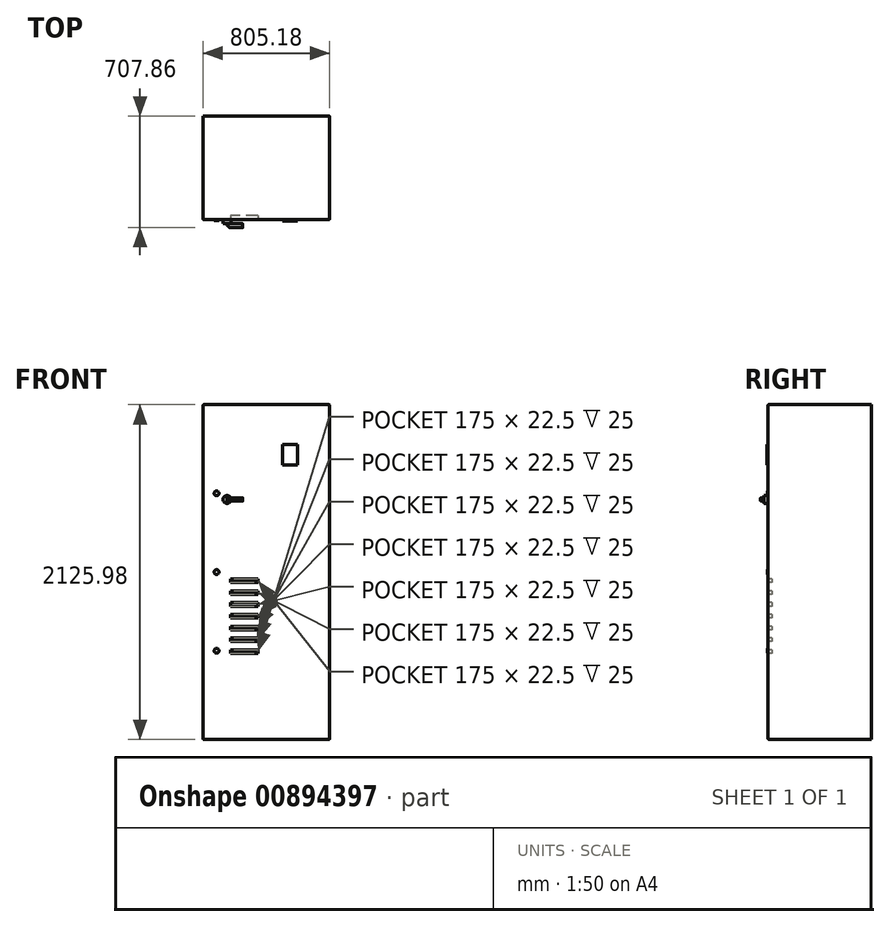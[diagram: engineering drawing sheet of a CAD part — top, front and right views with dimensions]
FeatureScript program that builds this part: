
annotation { "Feature Type Name" : "Feature", "Feature Type Description" : "" }
export const myFeature = defineFeature(function(context is Context, id is Id, definition is map)
    precondition{}
    {
        {
            var Q0;
            Q0=qCreatedBy(makeId("Front.planeOp"),FACE);
            var sketch = newSketch(context, id + "F0", { "sketchPlane" : qUnion([Q0])});
            skLineSegment(sketch, "E0.bottom", {"start": v(402.6, 1063) * mm, "end": v(-402.59, 1063) * mm});
            skLineSegment(sketch, "E0.top", {"start": v(402.59, -1063) * mm, "end": v(-402.6, -1063) * mm});
            skLineSegment(sketch, "E0.left", {"start": v(402.6, 1063) * mm, "end": v(402.59, -1063) * mm});
            skLineSegment(sketch, "E0.right", {"start": v(-402.59, 1063) * mm, "end": v(-402.6, -1063) * mm});
            skPoint(sketch, "E0.middle", {"position": v(0, 0) * mm});
            skSolve(sketch);
        }
        {
            var Q0;
            Q0 = qSketchRegion(id + "F0", true);
            extrude(context, id + "F1", {"entities" : qUnion([Q0]), "depth" : 657.86 * mm, "offsetDistance" : 25 * mm});
        }
        {
            var Q0;
            Q0=makeQuery(id+"F1.opExtrude","CAP_FACE",FACE,{"disambiguationData":[OSD([sQuery(id+"F0.wireOp",EDGE,"E0.bottom"),sQuery(id+"F0.wireOp",EDGE,"E0.top"),sQuery(id+"F0.wireOp",EDGE,"E0.left"),sQuery(id+"F0.wireOp",EDGE,"E0.right")])],"isStart":false});
            var sketch = newSketch(context, id + "F2", { "sketchPlane" : qUnion([Q0])});
            skCircle(sketch, "E1", {"center": v(-250.19, 461.01) * mm, "radius": 25 * mm});
            skSolve(sketch);
        }
        {
            var Q0;
            Q0 = qSketchRegion(id + "F2", true);
            extrude(context, id + "F3", {"entities" : qUnion([Q0]), "depth" : 25 * mm, "offsetDistance" : 25 * mm});
        }
        {
            var Q0;
            Q0=makeQuery(id+"F3.opExtrude","CAP_FACE",FACE,{"disambiguationData":[OSD([sQuery(id+"F2.wireOp",EDGE,"E1")])],"isStart":false});
            var sketch = newSketch(context, id + "F4", { "sketchPlane" : qUnion([Q0])});
            skLineSegment(sketch, "E2", {"start": v(-250.19, 461.01) * mm, "end": v(-250.19, 471.01) * mm});
            skLineSegment(sketch, "E3", {"start": v(-250.19, 471.01) * mm, "end": v(-149.7, 471.01) * mm});
            skLineSegment(sketch, "E4", {"start": v(-149.7, 471.01) * mm, "end": v(-149.7, 451.01) * mm});
            skLineSegment(sketch, "E5", {"start": v(-149.7, 451.01) * mm, "end": v(-250.19, 451.01) * mm});
            skLineSegment(sketch, "E6", {"start": v(-250.19, 451.01) * mm, "end": v(-250.19, 461.01) * mm});
            skSolve(sketch);
        }
        {
            var Q0;
            Q0 = qSketchRegion(id + "F4", true);
            extrude(context, id + "F5", {"entities" : qUnion([Q0]), "operationType" : NewBodyOperationType.ADD, "depth" : 25 * mm, "offsetDistance" : 25 * mm});
        }
        {
            var Q0;
            Q0=makeQuery(id+"F5.opExtrude","CAP_EDGE",EDGE,{"disambiguationData":[OSD([sQuery(id+"F4.wireOp",EDGE,"E2"),sQuery(id+"F4.wireOp",EDGE,"E6")])],"isStart":false});
            chamfer(context, id + "F6", {"entities" : qUnion([Q0]), "width" : 15 * mm, "tangentPropagation" : true});
        }
        {
            var Q0;
            {var subQ0=sQuery(id+"F4.wireOp",EDGE,"E5");Q0=makeQuery(id+"F5.boolean.opBoolean","SPLIT",EDGE,{"disambiguationData":[topologyDisambiguationEdgeConnected([makeQuery(id+"F3.opExtrude","CAP_FACE",FACE,{"disambiguationData":[OSD([sQuery(id+"F2.wireOp",EDGE,"E1")])],"isStart":false})])],"derivedFrom":makeQuery(id+"F5.opExtrude","CAP_EDGE",EDGE,{"disambiguationData":[OSD([subQ0])],"isStart":true})});}
            var Q1;
            Q1=makeQuery(id+"F5.opExtrude","CAP_EDGE",EDGE,{"disambiguationData":[OSD([sQuery(id+"F4.wireOp",EDGE,"E2"),sQuery(id+"F4.wireOp",EDGE,"E6")])],"isStart":true});
            var Q2;
            {var subQ0=sQuery(id+"F4.wireOp",EDGE,"E3");Q2=makeQuery(id+"F5.boolean.opBoolean","SPLIT",EDGE,{"disambiguationData":[topologyDisambiguationEdgeConnected([makeQuery(id+"F3.opExtrude","CAP_FACE",FACE,{"disambiguationData":[OSD([sQuery(id+"F2.wireOp",EDGE,"E1")])],"isStart":false})])],"derivedFrom":makeQuery(id+"F5.opExtrude","CAP_EDGE",EDGE,{"disambiguationData":[OSD([subQ0])],"isStart":true})});}
            var Q3;
            Q3=makeQuery(id+"F5.opExtrude","CAP_EDGE",EDGE,{"disambiguationData":[OSD([sQuery(id+"F4.wireOp",EDGE,"E3")])],"isStart":false});
            var Q4;
            Q4=makeQuery(id+"F5.opExtrude","CAP_EDGE",EDGE,{"disambiguationData":[OSD([sQuery(id+"F4.wireOp",EDGE,"E5")])],"isStart":false});
            var Q5;
            {var subQ0=sQuery(id+"F4.wireOp",EDGE,"E6");var subQ1=sQuery(id+"F4.wireOp",EDGE,"E2");Q5=makeQuery(id+"F6.opChamfer","BLEND_EDGE",EDGE,{"blendedFrom":[makeQuery(id+"F5.opExtrude","CAP_EDGE",EDGE,{"disambiguationData":[OSD([subQ1,subQ0])],"isStart":false}),makeQuery(id+"F5.opExtrude","CAP_FACE",FACE,{"disambiguationData":[OSD([subQ1,sQuery(id+"F4.wireOp",EDGE,"E3"),sQuery(id+"F4.wireOp",EDGE,"E4"),sQuery(id+"F4.wireOp",EDGE,"E5"),subQ0])],"isStart":false})],"blendedInto":[makeQuery(id+"F5.opExtrude","CAP_FACE",FACE,{"disambiguationData":[OSD([subQ1,sQuery(id+"F4.wireOp",EDGE,"E3"),sQuery(id+"F4.wireOp",EDGE,"E4"),sQuery(id+"F4.wireOp",EDGE,"E5"),subQ0])],"isStart":false})]});}
            var Q6;
            {var subQ0=sQuery(id+"F4.wireOp",EDGE,"E6");var subQ1=sQuery(id+"F4.wireOp",EDGE,"E2");Q6=makeQuery(id+"F6.opChamfer","BLEND_EDGE",EDGE,{"blendedFrom":[makeQuery(id+"F5.opExtrude","CAP_EDGE",EDGE,{"disambiguationData":[OSD([subQ1,subQ0])],"isStart":false}),makeQuery(id+"F5.opExtrude","SWEPT_FACE",FACE,{"disambiguationData":[OSD([subQ1,subQ0])]})],"blendedInto":[makeQuery(id+"F5.opExtrude","SWEPT_FACE",FACE,{"disambiguationData":[OSD([subQ1,subQ0])]})]});}
            fillet(context, id + "F7", {"entities" : qUnion([Q0, Q1, Q2, Q3, Q4, Q5, Q6]), "radius" : 5 * mm, "tangentPropagation" : true, "allowEdgeOverflow" : false});
        }
        {
            var Q0;
            Q0=makeQuery(id+"F1.opExtrude","CAP_FACE",FACE,{"disambiguationData":[OSD([sQuery(id+"F0.wireOp",EDGE,"E0.bottom"),sQuery(id+"F0.wireOp",EDGE,"E0.top"),sQuery(id+"F0.wireOp",EDGE,"E0.left"),sQuery(id+"F0.wireOp",EDGE,"E0.right")])],"isStart":true});
            var sketch = newSketch(context, id + "F8", { "sketchPlane" : qUnion([Q0])});
            skLineSegment(sketch, "E7.bottom", {"start": v(356.25, 606) * mm, "end": v(300, 606) * mm});
            skLineSegment(sketch, "E7.top", {"start": v(356.25, -606) * mm, "end": v(305, -606) * mm});
            skLineSegment(sketch, "E7.left", {"start": v(356.25, 606) * mm, "end": v(356.25, -606) * mm});
            skLineSegment(sketch, "E7.right", {"start": v(-356.25, 606) * mm, "end": v(-356.25, -606) * mm});
            skPoint(sketch, "E7.middle", {"position": v(0, 0) * mm});
            skLineSegment(sketch, "E8", {"start": v(0, 665.64) * mm, "end": v(0, -668.18) * mm, "construction": true});
            skLineSegment(sketch, "E9.bottom", {"start": v(300, 647.98) * mm, "end": v(-300, 647.98) * mm, "construction": true});
            skLineSegment(sketch, "E9.top", {"start": v(300, -647.98) * mm, "end": v(-300, -647.98) * mm, "construction": true});
            skLineSegment(sketch, "E9.left", {"start": v(300, 647.98) * mm, "end": v(300, -647.98) * mm, "construction": true});
            skLineSegment(sketch, "E9.right", {"start": v(-300, 647.98) * mm, "end": v(-300, -647.98) * mm, "construction": true});
            skLineSegment(sketch, "E10.left", {"start": v(-295, -606) * mm, "end": v(-295, -591) * mm});
            skLineSegment(sketch, "E10.right", {"start": v(-305, -606) * mm, "end": v(-305, -591) * mm});
            skPoint(sketch, "E10.middle", {"position": v(-300, -598.5) * mm});
            skArc(sketch, "E11", {"start": v(-305, -591) * mm, "mid": v(-300, -586) * mm, "end": v(-295, -591) * mm});
            skLineSegment(sketch, "E12.trimOffspring", {"start": v(-305, -606) * mm, "end": v(-356.25, -606) * mm});
            skLineSegment(sketch, "E13.MirrorCS", {"start": v(295, -606) * mm, "end": v(300, -606) * mm});
            skLineSegment(sketch, "E14.MirrorCS", {"start": v(305, -606) * mm, "end": v(305, -591) * mm});
            skLineSegment(sketch, "E15.MirrorCS", {"start": v(300, -606) * mm, "end": v(295, -606) * mm});
            skArc(sketch, "E16.MirrorCS", {"start": v(305, -591) * mm, "mid": v(300, -586) * mm, "end": v(295, -591) * mm});
            skLineSegment(sketch, "E17.MirrorCS", {"start": v(295, -606) * mm, "end": v(295, -591) * mm});
            skPoint(sketch, "E18.MirrorP", {"position": v(300, -598.5) * mm});
            skLineSegment(sketch, "E19.MirrorCS", {"start": v(-300, 606) * mm, "end": v(-305, 606) * mm});
            skLineSegment(sketch, "E20.MirrorCS", {"start": v(305, 606) * mm, "end": v(300, 606) * mm});
            skArc(sketch, "E21.MirrorCS", {"start": v(305, 591) * mm, "mid": v(300, 586) * mm, "end": v(295, 591) * mm});
            skLineSegment(sketch, "E22.MirrorCS", {"start": v(295, 606) * mm, "end": v(295, 591) * mm});
            skArc(sketch, "E23.MirrorCS", {"start": v(-305, 591) * mm, "mid": v(-300, 586) * mm, "end": v(-295, 591) * mm});
            skLineSegment(sketch, "E24.MirrorCS", {"start": v(-305, 606) * mm, "end": v(-305, 591) * mm});
            skLineSegment(sketch, "E25.MirrorCS", {"start": v(300, 606) * mm, "end": v(305, 606) * mm});
            skLineSegment(sketch, "E26.MirrorCS", {"start": v(-305, 606) * mm, "end": v(-300, 606) * mm});
            skLineSegment(sketch, "E27.MirrorCS", {"start": v(-295, 606) * mm, "end": v(-295, 591) * mm});
            skLineSegment(sketch, "E28.MirrorCS", {"start": v(305, 606) * mm, "end": v(305, 591) * mm});
            skPoint(sketch, "E29.MirrorP", {"position": v(300, 598.5) * mm});
            skPoint(sketch, "E30.MirrorP", {"position": v(-300, 598.5) * mm});
            skLineSegment(sketch, "E31.trimOffspring", {"start": v(300, -606) * mm, "end": v(-295, -606) * mm});
            skLineSegment(sketch, "E32.trimOffspring", {"start": v(295, 606) * mm, "end": v(-295, 606) * mm});
            skLineSegment(sketch, "E33.trimOffspring", {"start": v(-300, 606) * mm, "end": v(-356.25, 606) * mm});
            skPoint(sketch, "E34.orphan", {"position": v(-295, 606) * mm});
            skSolve(sketch);
        }
        {
            var Q0;
            Q0=makeQuery(id+"F1.opExtrude","CAP_FACE",FACE,{"disambiguationData":[OSD([sQuery(id+"F0.wireOp",EDGE,"E0.bottom"),sQuery(id+"F0.wireOp",EDGE,"E0.top"),sQuery(id+"F0.wireOp",EDGE,"E0.left"),sQuery(id+"F0.wireOp",EDGE,"E0.right")])],"isStart":false});
            var sketch = newSketch(context, id + "F9", { "sketchPlane" : qUnion([Q0])});
            skLineSegment(sketch, "E35.bottom", {"start": v(199.39, 809) * mm, "end": v(103.48, 809) * mm});
            skLineSegment(sketch, "E35.top", {"start": v(199.39, 681.5) * mm, "end": v(103.48, 681.5) * mm});
            skLineSegment(sketch, "E35.left", {"start": v(199.4, 809) * mm, "end": v(199.4, 681.5) * mm});
            skLineSegment(sketch, "E35.right", {"start": v(103.48, 809) * mm, "end": v(103.48, 681.5) * mm});
            skPoint(sketch, "E35.middle", {"position": v(151.43, 745.25) * mm});
            skSolve(sketch);
        }
        {
            var Q0;
            Q0 = qSketchRegion(id + "F9", true);
            extrude(context, id + "F10", {"entities" : qUnion([Q0]), "depth" : 7.5 * mm, "offsetDistance" : 25 * mm});
        }
        {
            var Q0;
            Q0=makeQuery(id+"F1.opExtrude","CAP_FACE",FACE,{"disambiguationData":[OSD([sQuery(id+"F0.wireOp",EDGE,"E0.bottom"),sQuery(id+"F0.wireOp",EDGE,"E0.top"),sQuery(id+"F0.wireOp",EDGE,"E0.left"),sQuery(id+"F0.wireOp",EDGE,"E0.right")])],"isStart":false});
            var sketch = newSketch(context, id + "F11", { "sketchPlane" : qUnion([Q0])});
            skLineSegment(sketch, "E36.bottom", {"start": v(-53.17, -44.51) * mm, "end": v(-228.17, -44.51) * mm});
            skLineSegment(sketch, "E36.top", {"start": v(-53.17, -67.01) * mm, "end": v(-228.17, -67.01) * mm});
            skLineSegment(sketch, "E36.left", {"start": v(-53.17, -44.51) * mm, "end": v(-53.17, -67.01) * mm});
            skLineSegment(sketch, "E36.right", {"start": v(-228.17, -44.51) * mm, "end": v(-228.17, -67.01) * mm});
            skPoint(sketch, "E36.middle", {"position": v(-140.67, -55.76) * mm});
            skLineSegment(sketch, "E37.0.1.0", {"start": v(-53.17, -142.01) * mm, "end": v(-228.17, -142.01) * mm});
            skLineSegment(sketch, "E37.0.1.1", {"start": v(-53.17, -119.51) * mm, "end": v(-228.17, -119.51) * mm});
            skLineSegment(sketch, "E37.0.1.2", {"start": v(-53.17, -119.51) * mm, "end": v(-53.17, -142.01) * mm});
            skLineSegment(sketch, "E37.0.1.3", {"start": v(-228.17, -119.51) * mm, "end": v(-228.17, -142.01) * mm});
            skLineSegment(sketch, "E37.0.2.0", {"start": v(-53.17, -217.01) * mm, "end": v(-228.17, -217.01) * mm});
            skLineSegment(sketch, "E37.0.2.1", {"start": v(-53.17, -194.51) * mm, "end": v(-228.17, -194.51) * mm});
            skLineSegment(sketch, "E37.0.2.2", {"start": v(-53.17, -194.51) * mm, "end": v(-53.17, -217.01) * mm});
            skLineSegment(sketch, "E37.0.2.3", {"start": v(-228.17, -194.51) * mm, "end": v(-228.17, -217.01) * mm});
            skLineSegment(sketch, "E37.0.3.0", {"start": v(-53.17, -292.01) * mm, "end": v(-228.17, -292.01) * mm});
            skLineSegment(sketch, "E37.0.3.1", {"start": v(-53.17, -269.51) * mm, "end": v(-228.17, -269.51) * mm});
            skLineSegment(sketch, "E37.0.3.2", {"start": v(-53.17, -269.51) * mm, "end": v(-53.17, -292.01) * mm});
            skLineSegment(sketch, "E37.0.3.3", {"start": v(-228.17, -269.51) * mm, "end": v(-228.17, -292.01) * mm});
            skLineSegment(sketch, "E37.0.4.0", {"start": v(-53.17, -367.01) * mm, "end": v(-228.17, -367.01) * mm});
            skLineSegment(sketch, "E37.0.4.1", {"start": v(-53.17, -344.51) * mm, "end": v(-228.17, -344.51) * mm});
            skLineSegment(sketch, "E37.0.4.2", {"start": v(-53.17, -344.51) * mm, "end": v(-53.17, -367.01) * mm});
            skLineSegment(sketch, "E37.0.4.3", {"start": v(-228.17, -344.51) * mm, "end": v(-228.17, -367.01) * mm});
            skLineSegment(sketch, "E37.0.5.0", {"start": v(-53.17, -442.01) * mm, "end": v(-228.17, -442.01) * mm});
            skLineSegment(sketch, "E37.0.5.1", {"start": v(-53.17, -419.51) * mm, "end": v(-228.17, -419.51) * mm});
            skLineSegment(sketch, "E37.0.5.2", {"start": v(-53.17, -419.51) * mm, "end": v(-53.17, -442.01) * mm});
            skLineSegment(sketch, "E37.0.5.3", {"start": v(-228.17, -419.51) * mm, "end": v(-228.17, -442.01) * mm});
            skLineSegment(sketch, "E37.0.6.0", {"start": v(-53.17, -517.01) * mm, "end": v(-228.17, -517.01) * mm});
            skLineSegment(sketch, "E37.0.6.1", {"start": v(-53.17, -494.51) * mm, "end": v(-228.17, -494.51) * mm});
            skLineSegment(sketch, "E37.0.6.2", {"start": v(-53.17, -494.51) * mm, "end": v(-53.17, -517.01) * mm});
            skLineSegment(sketch, "E37.0.6.3", {"start": v(-228.17, -494.51) * mm, "end": v(-228.17, -517.01) * mm});
            skLineSegment(sketch, "E37.direction1", {"start": v(-228.17, -67.01) * mm, "end": v(-203.17, -67.01) * mm, "construction": true});
            skLineSegment(sketch, "E37.direction2", {"start": v(-228.17, -67.01) * mm, "end": v(-228.17, -142.01) * mm, "construction": true});
            skSolve(sketch);
        }
        {
            var Q0;
            Q0 = qSketchRegion(id + "F11", true);
            extrude(context, id + "F12", {"entities" : qUnion([Q0]), "operationType" : NewBodyOperationType.REMOVE, "oppositeDirection" : true, "depth" : 25 * mm, "offsetDistance" : 25 * mm});
        }
        {
            var Q0;
            Q0=makeQuery(id+"F1.opExtrude","SWEPT_EDGE",EDGE,{"disambiguationData":[OSD([sQuery(id+"F0.wireOp",EDGE,"E0.bottom"),sQuery(id+"F0.wireOp",EDGE,"E0.right")])]});
            var Q1;
            Q1=makeQuery(id+"F1.opExtrude","SWEPT_EDGE",EDGE,{"disambiguationData":[OSD([sQuery(id+"F0.wireOp",EDGE,"E0.bottom"),sQuery(id+"F0.wireOp",EDGE,"E0.left")])]});
            var Q2;
            Q2=makeQuery(id+"F1.opExtrude","CAP_EDGE",EDGE,{"disambiguationData":[OSD([sQuery(id+"F0.wireOp",EDGE,"E0.bottom")])],"isStart":false});
            var Q3;
            Q3=makeQuery(id+"F1.opExtrude","CAP_EDGE",EDGE,{"disambiguationData":[OSD([sQuery(id+"F0.wireOp",EDGE,"E0.left")])],"isStart":false});
            var Q4;
            Q4=makeQuery(id+"F1.opExtrude","CAP_EDGE",EDGE,{"disambiguationData":[OSD([sQuery(id+"F0.wireOp",EDGE,"E0.right")])],"isStart":false});
            var Q5;
            Q5=makeQuery(id+"F1.opExtrude","SWEPT_EDGE",EDGE,{"disambiguationData":[OSD([sQuery(id+"F0.wireOp",EDGE,"E0.top"),sQuery(id+"F0.wireOp",EDGE,"E0.right")])]});
            var Q6;
            Q6=makeQuery(id+"F1.opExtrude","CAP_EDGE",EDGE,{"disambiguationData":[OSD([sQuery(id+"F0.wireOp",EDGE,"E0.top")])],"isStart":false});
            var Q7;
            Q7=makeQuery(id+"F1.opExtrude","SWEPT_EDGE",EDGE,{"disambiguationData":[OSD([sQuery(id+"F0.wireOp",EDGE,"E0.top"),sQuery(id+"F0.wireOp",EDGE,"E0.left")])]});
            fillet(context, id + "F13", {"entities" : qUnion([Q0, Q1, Q2, Q3, Q4, Q5, Q6, Q7]), "radius" : 5 * mm, "tangentPropagation" : true, "allowEdgeOverflow" : false});
        }
        {
            var Q0;
            Q0=makeQuery(id+"F1.opExtrude","CAP_FACE",FACE,{"disambiguationData":[OSD([sQuery(id+"F0.wireOp",EDGE,"E0.bottom"),sQuery(id+"F0.wireOp",EDGE,"E0.top"),sQuery(id+"F0.wireOp",EDGE,"E0.left"),sQuery(id+"F0.wireOp",EDGE,"E0.right")])],"isStart":false});
            var sketch = newSketch(context, id + "F14", { "sketchPlane" : qUnion([Q0])});
            skCircle(sketch, "E38", {"center": v(-316.07, 0) * mm, "radius": 15 * mm});
            skPoint(sketch, "E38.centerSnap0", {"position": v(-397.59, 0) * mm});
            skCircle(sketch, "E39", {"center": v(-316.07, -500) * mm, "radius": 15 * mm});
            skCircle(sketch, "E40", {"center": v(-316.07, 500) * mm, "radius": 15 * mm});
            skSolve(sketch);
        }
        {
            var Q0;
            Q0 = qSketchRegion(id + "F14", true);
            extrude(context, id + "F15", {"entities" : qUnion([Q0]), "depth" : 5 * mm, "offsetDistance" : 25 * mm});
        }
    });
